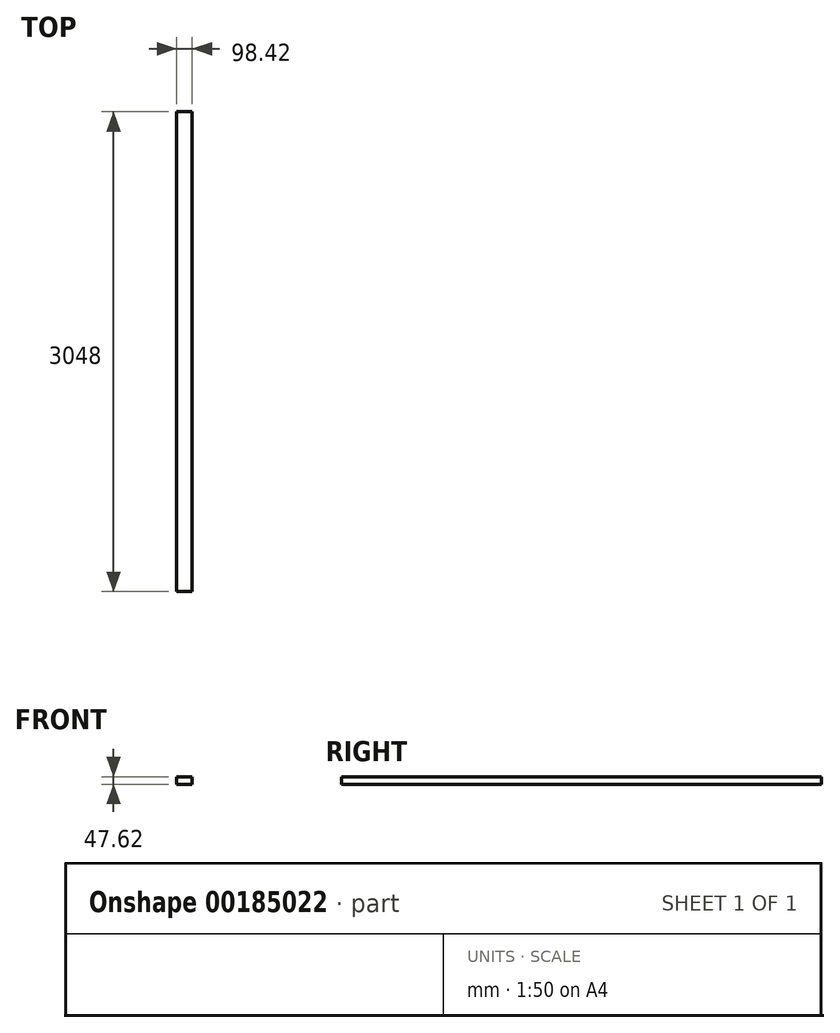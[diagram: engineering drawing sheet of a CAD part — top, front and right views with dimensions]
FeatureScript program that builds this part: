
annotation { "Feature Type Name" : "Feature", "Feature Type Description" : "" }
export const myFeature = defineFeature(function(context is Context, id is Id, definition is map)
    precondition{}
    {
        {
            var Q0;
            Q0=qCreatedBy(makeId("Front.planeOp"),FACE);
            var sketch = newSketch(context, id + "F0", { "sketchPlane" : qUnion([Q0])});
            skLineSegment(sketch, "E0.bottom", {"start": v(49.21, 23.81) * mm, "end": v(-49.21, 23.81) * mm});
            skLineSegment(sketch, "E0.top", {"start": v(49.21, -23.81) * mm, "end": v(-49.21, -23.81) * mm});
            skLineSegment(sketch, "E0.left", {"start": v(49.21, 23.81) * mm, "end": v(49.21, -23.81) * mm});
            skLineSegment(sketch, "E0.right", {"start": v(-49.21, 23.81) * mm, "end": v(-49.21, -23.81) * mm});
            skPoint(sketch, "E0.middle", {"position": v(0, 0) * mm});
            skSolve(sketch);
        }
        {
            var Q0;
            Q0=makeQuery(id+"F0.imprint","IMPRINT",FACE,{"disambiguationData":[TD([[makeQuery(id+"F0.imprint","IMPRINT",EDGE,{"derivedFrom":sQuery(id+"F0.wireOp",EDGE,"E0.bottom")}),1.0]])]});
            extrude(context, id + "F1", {"entities" : qUnion([Q0]), "depth" : 3048 * mm});
        }
    });
